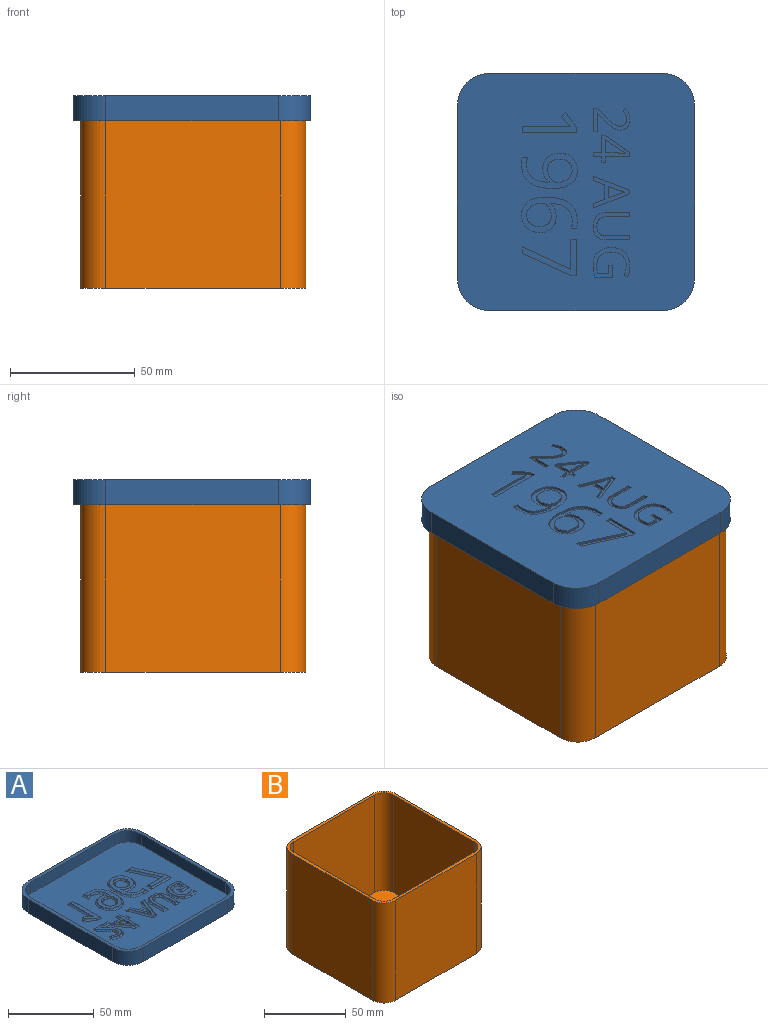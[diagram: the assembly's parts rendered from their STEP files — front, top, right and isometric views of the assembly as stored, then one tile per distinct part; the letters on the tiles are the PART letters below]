
ASSEMBLY  parts=2 mates=1
PART A: 347 faces, bbox 96x96x11 mm
  f0: plane 95x95mm, normal (0,0,-1), area 8042.6mm2, adj f2,f3,f4,f5,f6,f7,f8,f17
  f1: plane 91x91mm, normal (0,0,1), area 6700.1mm2, adj f9,f10,f11,f12,f13,f14,f15,f16
  f2: plane 69x10mm, normal (1,0,0), area 690mm2, adj f0,f3,f17,f18
  f3: cylinder r=13mm len=13mm, axis (0,0,-1), area 204.2mm2, adj f0,f2,f4,f18
  f4: plane 69x10mm, normal (0,1,0), area 690mm2, adj f0,f3,f5,f18
  f5: cylinder r=13mm len=13mm, axis (0,0,-1), area 204.2mm2, adj f0,f4,f6,f18
  f6: plane 69x10mm, normal (-1,0,0), area 690mm2, adj f0,f5,f7,f18
  f7: cylinder r=13mm len=13mm, axis (0,0,-1), area 204.2mm2, adj f0,f6,f8,f18
  f8: plane 69x10mm, normal (0,-1,0), area 690mm2, adj f0,f7,f17,f18
  f9: cylinder r=11mm len=11mm, axis (0,0,-1), area 138.2mm2, adj f1,f10,f16,f18
  f10: plane 69x8mm, normal (-1,0,0), area 552mm2, adj f1,f9,f11,f18
  f11: cylinder r=11mm len=11mm, axis (0,0,-1), area 138.2mm2, adj f1,f10,f12,f18
  f12: plane 69x8mm, normal (0,1,0), area 552mm2, adj f1,f11,f13,f18
  f13: cylinder r=11mm len=11mm, axis (0,0,-1), area 138.2mm2, adj f1,f12,f14,f18
  f14: plane 69x8mm, normal (1,0,0), area 552mm2, adj f1,f13,f15,f18
  f15: cylinder r=11mm len=11mm, axis (0,0,-1), area 138.2mm2, adj f1,f14,f16,f18
  f16: plane 69x8mm, normal (0,-1,0), area 552mm2, adj f1,f9,f15,f18
  f17: cylinder r=13mm len=13mm, axis (0,0,-1), area 204.2mm2, adj f0,f2,f8,f18
  f18: plane 95x95mm, normal (0,0,1), area 702.8mm2, adj f2,f3,f4,f5,f6,f7,f8,f9
  f19: plane 0.27x0.09mm, normal (1,0,0), area 0mm2, adj f20,f247,f249
  f20: plane 15.41x10.28mm, normal (0,0,1), area 45.3mm2, adj f19,f243,f246,f247,f248,f249,f250,f251
  f21: plane 5.35x1mm, normal (0,-1,0), area 5.3mm2, adj f22,f26,f27,f28
  f22: plane 6.38x4.48mm, normal (0.82,0.58,0), area 7.8mm2, adj f21,f23,f27,f28
  f23: extruded ~1.56x1mm, area 1.8mm2, adj f22,f24,f27,f28
  f24: plane 1x0.08mm, normal (0,1,0), area 0.1mm2, adj f23,f25,f27,f28
  f25: extruded ~3.17x1mm, area 3.2mm2, adj f24,f26,f27,f28
  f26: plane 4.77x1mm, normal (-1,0,0), area 4.8mm2, adj f21,f25,f27,f28
  f27: plane 14.42x10.67mm, normal (0,0,1), area 49.7mm2, adj f21,f22,f23,f24,f25,f26,f234,f235
  f28: plane 7.94x5.45mm, normal (0,0,1), area 20.5mm2, adj f21,f22,f23,f24,f25,f26
  f29: plane 14.5x12.81mm, normal (0,0,1), area 52.9mm2, adj f334,f335,f336,f337,f338,f339,f340,f341
  f30: plane 2.32x1.75mm, normal (0,0,1), area 2mm2, adj f344,f345,f346
  f31: plane 15.08x11.51mm, normal (0,0,1), area 54.1mm2, adj f284,f285,f286,f287,f288,f289,f290,f291
  f32: plane 15.42x12.61mm, normal (0,0,1), area 62.3mm2, adj f298,f299,f300,f301,f302,f303,f304,f305
  f33: plane 21.82x7.92mm, normal (0,0,1), area 64.6mm2, adj f318,f319,f320,f321,f322,f323,f324,f325
  f34: plane 0.42x0.21mm, normal (0,1,0), area 0mm2, adj f35,f223,f225
  f35: plane 22.92x14.78mm, normal (0,0,1), area 122.3mm2, adj f34,f219,f220,f221,f222,f223,f224,f225
  f36: plane 7.76x7.26mm, normal (0,0,1), area 45.7mm2, adj f274,f275,f276,f277,f278,f279,f280,f281
  f37: plane 0.42x0.2mm, normal (0,-1,0), area 0mm2, adj f38,f208,f210
  f38: plane 23.33x15.17mm, normal (0,0,1), area 122.1mm2, adj f37,f205,f206,f207,f208,f209,f210,f211
  f39: plane 7.79x7.21mm, normal (0,0,1), area 45.5mm2, adj f264,f265,f266,f267,f268,f269,f270,f271
  f40: plane 21.72x14.45mm, normal (0,0,1), area 83.5mm2, adj f327,f328,f329,f330,f331,f332,f333
  f41: plane 1.51x1mm, normal (-1,0,0), area 1.5mm2, adj f0,f42,f60,f61
  f42: plane 7.38x1mm, normal (0,1,0), area 7.4mm2, adj f0,f41,f43,f61
  f43: plane 1x0.08mm, normal (-1,0,0), area 0.1mm2, adj f0,f42,f44,f61
  f44: plane 3.14x3.07mm, normal (-0.7,-0.71,0), area 4.4mm2, adj f0,f43,f45,f61
  f45: extruded ~3.38x2.86mm, area 4.4mm2, adj f0,f44,f46,f61
  f46: extruded ~2.7x1mm, area 2.8mm2, adj f0,f45,f47,f61
  f47: extruded ~2.78x1.15mm, area 3.1mm2, adj f0,f46,f48,f61
  f48: extruded ~3.17x1.03mm, area 3.4mm2, adj f0,f47,f49,f61
  f49: extruded ~4.32x1.65mm, area 4.7mm2, adj f0,f48,f50,f61
  f50: plane 1.11x1mm, normal (0.79,-0.61,0), area 1.4mm2, adj f0,f49,f51,f61
  f51: extruded ~1.78x1.07mm, area 2.1mm2, adj f0,f50,f52,f61
  f52: extruded ~1.69x1mm, area 1.7mm2, adj f0,f51,f53,f61
  f53: extruded ~1.93x1mm, area 2.1mm2, adj f0,f52,f54,f61
  f54: extruded ~1.82x1mm, area 2mm2, adj f0,f53,f55,f61
  f55: extruded ~1.52x1mm, area 1.6mm2, adj f0,f54,f56,f61
  f56: extruded ~1.45x1mm, area 1.7mm2, adj f0,f55,f57,f61
  f57: extruded ~2.49x2.28mm, area 3.4mm2, adj f0,f56,f58,f61
  f58: plane 3.8x3.78mm, normal (0.71,0.71,0), area 5.4mm2, adj f0,f57,f59,f61
  f59: plane 1.4x1mm, normal (1,0,0), area 1.4mm2, adj f0,f58,f60,f61
  f60: plane 9.43x1mm, normal (0,-1,0), area 9.4mm2, adj f0,f41,f59,f61
  f61: plane 14.55x9.43mm, normal (0,0,-1), area 45.3mm2, adj f41,f42,f43,f44,f45,f46,f47,f48
  f62: extruded ~7.05x1.98mm, area 7.5mm2, adj f0,f63,f86,f87
  f63: extruded ~5.35x2.53mm, area 6.1mm2, adj f0,f62,f64,f87
  f64: extruded ~5x1.94mm, area 5.5mm2, adj f0,f63,f65,f87
  f65: extruded ~5.33x1.85mm, area 5.8mm2, adj f0,f64,f66,f87
  f66: extruded ~4.8x1.69mm, area 5.2mm2, adj f0,f65,f67,f87
  f67: extruded ~4.61x1.77mm, area 5.1mm2, adj f0,f66,f68,f87
  f68: extruded ~5.17x2.56mm, area 6mm2, adj f0,f67,f69,f87
  f69: plane 1x0.18mm, normal (0,1,0), area 0.2mm2, adj f0,f68,f70,f87
  f70: extruded ~6.84x2.02mm, area 7.3mm2, adj f0,f69,f71,f87
  f71: extruded ~5.34x2.17mm, area 6mm2, adj f0,f70,f72,f87
  f72: extruded ~2.61x1mm, area 2.7mm2, adj f0,f71,f73,f87
  f73: plane 2.13x1mm, normal (-1,0,0), area 2.1mm2, adj f0,f72,f74,f87
  f74: extruded ~2.64x1mm, area 2.7mm2, adj f0,f73,f75,f87
  f75: extruded ~7.36x3.17mm, area 8.3mm2, adj f0,f74,f86,f87
  f76: extruded ~2.49x1mm, area 2.6mm2, adj f77,f85,f87,f88
  f77: extruded ~2.09x1.69mm, area 2.7mm2, adj f76,f78,f87,f88
  f78: extruded ~2.85x1mm, area 2.9mm2, adj f77,f79,f87,f88
  f79: extruded ~2.01x1mm, area 2.1mm2, adj f78,f80,f87,f88
  f80: extruded ~1.78x1.52mm, area 2.4mm2, adj f79,f81,f87,f88
  f81: extruded ~2.45x1mm, area 2.5mm2, adj f80,f82,f87,f88
  f82: extruded ~3.24x1.23mm, area 3.6mm2, adj f81,f83,f87,f88
  f83: extruded ~3.39x1.08mm, area 3.6mm2, adj f82,f84,f87,f88
  f84: extruded ~3.84x1.16mm, area 4.1mm2, adj f83,f85,f87,f88
  f85: extruded ~3.28x1.33mm, area 3.7mm2, adj f76,f84,f87,f88
  f86: extruded ~9.57x2.49mm, area 10.1mm2, adj f0,f62,f75,f87
  f87: plane 22.33x14.17mm, normal (0,0,-1), area 122.1mm2, adj f62,f63,f64,f65,f66,f67,f68,f69
  f88: plane 9.79x9.21mm, normal (0,0,-1), area 72.7mm2, adj f76,f77,f78,f79,f80,f81,f82,f83
  f89: extruded ~5.13x1mm, area 5.2mm2, adj f0,f90,f114,f115
  f90: extruded ~3.31x2.55mm, area 4.2mm2, adj f0,f89,f91,f115
  f91: extruded ~3.87x1.14mm, area 4.1mm2, adj f0,f90,f92,f115
  f92: extruded ~4.98x1.96mm, area 5.5mm2, adj f0,f91,f93,f115
  f93: extruded ~5.35x1.89mm, area 5.8mm2, adj f0,f92,f94,f115
  f94: extruded ~4.81x1.69mm, area 5.2mm2, adj f0,f93,f95,f115
  f95: extruded ~4.58x1.72mm, area 5mm2, adj f0,f94,f96,f115
  f96: extruded ~3.04x1mm, area 3.1mm2, adj f0,f95,f97,f115
  f97: extruded ~2.17x1.88mm, area 2.9mm2, adj f0,f96,f98,f115
  f98: plane 1x0.18mm, normal (0,-1,0), area 0.2mm2, adj f0,f97,f99,f115
  f99: extruded ~6.76x1.98mm, area 7.2mm2, adj f0,f98,f100,f115
  f100: extruded ~5.39x2.21mm, area 6mm2, adj f0,f99,f101,f115
  f101: extruded ~2.7x1mm, area 2.7mm2, adj f0,f100,f102,f115
  f102: plane 2.13x1mm, normal (1,0,0), area 2.1mm2, adj f0,f101,f103,f115
  f103: extruded ~2.73x1mm, area 2.8mm2, adj f0,f102,f114,f115
  f104: extruded ~2.5x1mm, area 2.7mm2, adj f105,f113,f115,f116
  f105: extruded ~2.08x1.7mm, area 2.7mm2, adj f104,f106,f115,f116
  f106: extruded ~2.88x1mm, area 3mm2, adj f105,f107,f115,f116
  f107: extruded ~1.99x1mm, area 2.1mm2, adj f106,f108,f115,f116
  f108: extruded ~1.79x1.5mm, area 2.4mm2, adj f107,f109,f115,f116
  f109: extruded ~2.49x1mm, area 2.6mm2, adj f108,f110,f115,f116
  f110: extruded ~3.25x1.22mm, area 3.6mm2, adj f109,f111,f115,f116
  f111: extruded ~3.36x1.07mm, area 3.6mm2, adj f110,f112,f115,f116
  f112: extruded ~3.81x1.16mm, area 4.1mm2, adj f111,f113,f115,f116
  f113: extruded ~3.28x1.37mm, area 3.7mm2, adj f104,f112,f115,f116
  f114: extruded ~12.75x9.86mm, area 18.4mm2, adj f0,f89,f103,f115
  f115: plane 22.33x14.19mm, normal (0,0,-1), area 122.3mm2, adj f89,f90,f91,f92,f93,f94,f95,f96
  f116: plane 9.76x9.26mm, normal (0,0,-1), area 72.9mm2, adj f104,f105,f106,f107,f108,f109,f110,f111
  f117: plane 1.73x1mm, normal (0,-1,0), area 1.7mm2, adj f0,f118,f129,f130
  f118: plane 14.4x5.64mm, normal (-0.93,0.36,0), area 15.5mm2, adj f0,f117,f119,f130
  f119: plane 1.4x1mm, normal (0,1,0), area 1.4mm2, adj f0,f118,f120,f130
  f120: plane 14.4x5.67mm, normal (0.93,0.37,0), area 15.5mm2, adj f0,f119,f121,f130
  f121: plane 1.69x1mm, normal (0,-1,0), area 1.7mm2, adj f0,f120,f122,f130
  f122: plane 4.56x1.76mm, normal (-0.93,-0.36,0), area 4.9mm2, adj f0,f121,f123,f130
  f123: plane 5.75x1mm, normal (0,-1,0), area 5.7mm2, adj f0,f122,f129,f130
  f124: plane 4.64x1mm, normal (0,1,0), area 4.6mm2, adj f125,f128,f130,f131
  f125: plane 4.45x1.69mm, normal (-0.94,-0.35,0), area 4.8mm2, adj f124,f126,f130,f131
  f126: extruded ~2.07x1mm, area 2.2mm2, adj f125,f127,f130,f131
  f127: extruded ~2.07x1mm, area 2.2mm2, adj f126,f128,f130,f131
  f128: plane 4.45x1.67mm, normal (0.94,-0.35,0), area 4.7mm2, adj f124,f127,f130,f131
  f129: plane 4.56x1.79mm, normal (0.93,-0.36,0), area 4.9mm2, adj f0,f117,f123,f130
  f130: plane 14.4x12.72mm, normal (0,0,-1), area 52.9mm2, adj f117,f118,f119,f120,f121,f122,f123,f124
  f131: plane 6.51x4.64mm, normal (0,0,-1), area 14.4mm2, adj f124,f125,f126,f127,f128
  f132: plane 1.48x1mm, normal (-1,0,0), area 1.5mm2, adj f0,f133,f148,f149
  f133: plane 2.13x1mm, normal (0,1,0), area 2.1mm2, adj f0,f132,f134,f149
  f134: plane 9.64x1mm, normal (-1,0,0), area 9.6mm2, adj f0,f133,f135,f149
  f135: plane 1.73x1mm, normal (0,1,0), area 1.7mm2, adj f0,f134,f136,f149
  f136: plane 9.7x6.81mm, normal (0.82,0.57,0), area 11.9mm2, adj f0,f135,f137,f149
  f137: plane 1.42x1mm, normal (1,0,0), area 1.4mm2, adj f0,f136,f138,f149
  f138: plane 6.98x1mm, normal (0,-1,0), area 7mm2, adj f0,f137,f139,f149
  f139: plane 3.3x1mm, normal (1,0,0), area 3.3mm2, adj f0,f138,f140,f149
  f140: plane 1.56x1mm, normal (0,-1,0), area 1.6mm2, adj f0,f139,f141,f149
  f141: plane 3.3x1mm, normal (-1,0,0), area 3.3mm2, adj f0,f140,f148,f149
  f142: plane 5.35x1mm, normal (0,1,0), area 5.3mm2, adj f143,f147,f149,f150
  f143: plane 6.38x4.48mm, normal (-0.82,-0.58,0), area 7.8mm2, adj f142,f144,f149,f150
  f144: extruded ~1.56x1mm, area 1.8mm2, adj f143,f145,f149,f150
  f145: plane 1x0.08mm, normal (0,-1,0), area 0.1mm2, adj f144,f146,f149,f150
  f146: extruded ~3.17x1mm, area 3.2mm2, adj f145,f147,f149,f150
  f147: plane 4.77x1mm, normal (1,0,0), area 4.8mm2, adj f142,f146,f149,f150
  f148: plane 2.13x1mm, normal (0,-1,0), area 2.1mm2, adj f0,f132,f141,f149
  f149: plane 14.42x10.67mm, normal (0,0,-1), area 49.7mm2, adj f132,f133,f134,f135,f136,f137,f138,f139
  f150: plane 7.94x5.45mm, normal (0,0,-1), area 20.5mm2, adj f142,f143,f144,f145,f146,f147
  f151: plane 2.73x1mm, normal (0,-1,0), area 2.7mm2, adj f0,f152,f157,f158
  f152: plane 19.74x8.88mm, normal (-0.91,-0.41,0), area 21.6mm2, adj f0,f151,f153,f158
  f153: plane 1.98x1mm, normal (-1,0,0), area 2mm2, adj f0,f152,f154,f158
  f154: plane 14.45x1mm, normal (0,1,0), area 14.5mm2, adj f0,f153,f155,f158
  f155: plane 2.27x1mm, normal (1,0,0), area 2.3mm2, adj f0,f154,f156,f158
  f156: plane 11.84x1mm, normal (0,-1,0), area 11.8mm2, adj f0,f155,f157,f158
  f157: plane 19.45x9mm, normal (0.91,0.42,0), area 21.4mm2, adj f0,f151,f156,f158
  f158: plane 21.72x14.45mm, normal (0,0,-1), area 83.5mm2, adj f151,f152,f153,f154,f155,f156,f157
  f159: plane 21.72x1mm, normal (-1,0,0), area 21.7mm2, adj f0,f160,f167,f168
  f160: plane 2.08x1mm, normal (0,1,0), area 2.1mm2, adj f0,f159,f161,f168
  f161: plane 5.75x4.44mm, normal (0.61,0.79,0), area 7.3mm2, adj f0,f160,f162,f168
  f162: plane 1.69x1.31mm, normal (0.79,-0.61,0), area 2.1mm2, adj f0,f161,f163,f168
  f163: extruded ~3.53x2.9mm, area 4.6mm2, adj f0,f162,f164,f168
  f164: extruded ~1x0.7mm, area 1mm2, adj f0,f163,f165,f168
  f165: extruded ~3.66x1mm, area 3.7mm2, adj f0,f164,f166,f168
  f166: plane 15.48x1mm, normal (1,0,0), area 15.5mm2, adj f0,f165,f167,f168
  f167: plane 2.41x1mm, normal (0,-1,0), area 2.4mm2, adj f0,f159,f166,f168
  f168: plane 21.72x7.82mm, normal (0,0,-1), area 64.6mm2, adj f159,f160,f161,f162,f163,f164,f165,f166
  f169: plane 1.49x1mm, normal (1,0,0), area 1.5mm2, adj f0,f170,f188,f189
  f170: plane 3.21x1mm, normal (0,-1,0), area 3.2mm2, adj f0,f169,f171,f189
  f171: plane 4.41x1mm, normal (1,0,0), area 4.4mm2, adj f0,f170,f172,f189
  f172: extruded ~2.91x1mm, area 2.9mm2, adj f0,f171,f173,f189
  f173: extruded ~4.16x1.5mm, area 4.6mm2, adj f0,f172,f174,f189
  f174: extruded ~4.41x1.42mm, area 4.7mm2, adj f0,f173,f175,f189
  f175: extruded ~4.33x1.47mm, area 4.7mm2, adj f0,f174,f176,f189
  f176: extruded ~4.09x1.56mm, area 4.5mm2, adj f0,f175,f177,f189
  f177: extruded ~3.74x1mm, area 3.9mm2, adj f0,f176,f178,f189
  f178: plane 1.47x1mm, normal (-0.92,-0.4,0), area 1.6mm2, adj f0,f177,f179,f189
  f179: extruded ~4.28x1mm, area 4.4mm2, adj f0,f178,f180,f189
  f180: extruded ~3.95x1mm, area 4.1mm2, adj f0,f179,f181,f189
  f181: extruded ~2.59x2.57mm, area 3.7mm2, adj f0,f180,f182,f189
  f182: extruded ~3.92x1mm, area 4.1mm2, adj f0,f181,f183,f189
  f183: extruded ~5.43x1.81mm, area 5.9mm2, adj f0,f182,f184,f189
  f184: extruded ~5.07x1.94mm, area 5.6mm2, adj f0,f183,f185,f189
  f185: extruded ~2.73x1mm, area 2.7mm2, adj f0,f184,f186,f189
  f186: extruded ~2.32x1mm, area 2.4mm2, adj f0,f185,f187,f189
  f187: plane 6.98x1mm, normal (-1,0,0), area 7mm2, adj f0,f186,f188,f189
  f188: plane 4.88x1mm, normal (0,1,0), area 4.9mm2, adj f0,f169,f187,f189
  f189: plane 14.75x11.93mm, normal (0,0,-1), area 62.3mm2, adj f169,f170,f171,f172,f173,f174,f175,f176
  f190: plane 1.67x1mm, normal (0,1,0), area 1.7mm2, adj f0,f191,f203,f204
  f191: plane 9.34x1mm, normal (1,0,0), area 9.3mm2, adj f0,f190,f192,f204
  f192: extruded ~2.77x1mm, area 3mm2, adj f0,f191,f193,f204
  f193: extruded ~2.8x1mm, area 3mm2, adj f0,f192,f194,f204
  f194: extruded ~2.88x1mm, area 3.1mm2, adj f0,f193,f195,f204
  f195: extruded ~2.76x1mm, area 3mm2, adj f0,f194,f196,f204
  f196: plane 9.36x1mm, normal (-1,0,0), area 9.4mm2, adj f0,f195,f197,f204
  f197: plane 1.67x1mm, normal (0,1,0), area 1.7mm2, adj f0,f196,f198,f204
  f198: plane 9.24x1mm, normal (1,0,0), area 9.2mm2, adj f0,f197,f199,f204
  f199: extruded ~3.89x1.42mm, area 4.2mm2, adj f0,f198,f200,f204
  f200: extruded ~4.01x1.41mm, area 4.4mm2, adj f0,f199,f201,f204
  f201: extruded ~4.07x1.4mm, area 4.4mm2, adj f0,f200,f202,f204
  f202: extruded ~3.86x1.48mm, area 4.3mm2, adj f0,f201,f203,f204
  f203: plane 9.28x1mm, normal (-1,0,0), area 9.3mm2, adj f0,f190,f202,f204
  f204: plane 14.54x10.98mm, normal (0,0,-1), area 54.1mm2, adj f190,f191,f192,f193,f194,f195,f196,f197
  f205: bspline ~7.95x3.31mm, area 8.6mm2, adj f1,f38,f206,f207
  f206: bspline ~8.05x3.93mm, area 8.5mm2, adj f1,f38,f205,f208
  f207: bspline ~7.27x3.56mm, area 9.5mm2, adj f1,f38,f205,f209
  f208: bspline ~8.69x4.94mm, area 8.6mm2, adj f1,f37,f38,f206,f210
  f209: bspline ~8.72x4.22mm, area 9.1mm2, adj f1,f38,f207,f211
  f210: bspline ~8.13x3.47mm, area 9.6mm2, adj f1,f37,f38,f208,f212
  f211: bspline ~8.86x4.86mm, area 10.2mm2, adj f1,f38,f209,f213
  f212: bspline ~8.24x4.17mm, area 8.9mm2, adj f1,f38,f210,f214
  f213: bspline ~9.63x3.21mm, area 12.1mm2, adj f1,f38,f211,f215
  f214: bspline ~5x2.04mm, area 5.1mm2, adj f1,f38,f212,f216
  f215: bspline ~14.26x4.89mm, area 16.2mm2, adj f1,f38,f213,f217
  f216: cylinder r=1mm len=4.25mm, axis (0,-1,0), area 5mm2, adj f1,f38,f214,f218
  f217: bspline ~12.1x6.09mm, area 13.6mm2, adj f1,f38,f215,f218
  f218: bspline ~6.77x2.18mm, area 4.9mm2, adj f1,f38,f216,f217
  f219: bspline ~7.06x2.86mm, area 8.3mm2, adj f1,f35,f220,f221
  f220: bspline ~7.93x3.32mm, area 8.7mm2, adj f1,f35,f219,f222
  f221: bspline ~4.22x1.93mm, area 5.2mm2, adj f1,f35,f219,f223
  f222: bspline ~7.28x3.6mm, area 9.6mm2, adj f1,f35,f220,f224
  f223: bspline ~4.08x3.72mm, area 3.5mm2, adj f1,f34,f35,f221,f225
  f224: bspline ~7.39x4.24mm, area 9.1mm2, adj f1,f35,f222,f226
  f225: bspline ~8.26x3.44mm, area 9.5mm2, adj f1,f34,f35,f223,f227
  f226: bspline ~5.99x2.62mm, area 6.8mm2, adj f1,f35,f224,f228
  f227: bspline ~6.96x4.2mm, area 9mm2, adj f1,f35,f225,f229
  f228: bspline ~5.47x4.55mm, area 7mm2, adj f1,f35,f226,f230
  f229: bspline ~5.64x2.06mm, area 5.2mm2, adj f1,f35,f227,f231
  f230: bspline ~7.55x2.29mm, area 8.5mm2, adj f1,f35,f228,f232
  f231: cylinder r=1mm len=4.25mm, axis (0,1,0), area 5mm2, adj f1,f35,f229,f233
  f232: bspline ~15.75x14.97mm, area 29.8mm2, adj f1,f35,f230,f233
  f233: bspline ~4.54x1.69mm, area 5.1mm2, adj f1,f35,f231,f232
  f234: cylinder r=1mm len=3.48mm, axis (0,-1,0), area 3.9mm2, adj f1,f27,f235,f236
  f235: cylinder r=1mm len=3.13mm, axis (1,0,0), area 3.3mm2, adj f1,f27,f234,f237
  f236: cylinder r=1mm len=3.13mm, axis (-1,0,0), area 3.3mm2, adj f1,f27,f234,f238
  f237: cylinder r=1mm len=4.3mm, axis (0,-1,0), area 5.2mm2, adj f1,f27,f235,f239
  f238: cylinder r=1mm len=10.64mm, axis (0,-1,0), area 15.1mm2, adj f1,f27,f236,f240
  f239: cylinder r=1mm len=3.56mm, axis (1,0,0), area 4mm2, adj f1,f27,f237,f241
  f240: cylinder r=1mm len=3.25mm, axis (-1,0,0), area 3.9mm2, adj f1,f27,f238,f242
  f241: cylinder r=1mm len=4.3mm, axis (0,1,0), area 5.2mm2, adj f1,f27,f239,f244
  f242: cylinder r=1mm len=10.96mm, axis (-0.57,0.82,0), area 19.3mm2, adj f1,f27,f240,f245
  f243: cylinder r=1mm len=3.4mm, axis (0,-1,0), area 3.5mm2, adj f1,f20,f244,f246,f247
  f244: cylinder r=1mm len=7.87mm, axis (1,0,0), area 10.9mm2, adj f1,f27,f241,f243,f245,f247
  f245: cylinder r=1mm len=2.63mm, axis (0,1,0), area 3mm2, adj f1,f27,f242,f244,f247
  f246: cylinder r=1mm len=11.43mm, axis (1,0,0), area 16.4mm2, adj f1,f20,f243,f248
  f247: cylinder r=1mm len=8.27mm, axis (-1,0,0), area 10.8mm2, adj f1,f19,f20,f243,f244,f245,f249
  f248: cylinder r=1mm len=2.82mm, axis (0,1,0), area 3.3mm2, adj f1,f20,f246,f250
  f249: cylinder r=1mm len=3.86mm, axis (0.71,-0.7,0), area 5.7mm2, adj f1,f19,f20,f247,f251
  f250: cylinder r=1mm len=4.79mm, axis (-0.71,0.71,0), area 8.7mm2, adj f1,f20,f248,f252
  f251: bspline ~5.26x4.73mm, area 7.1mm2, adj f1,f20,f249,f253
  f252: bspline ~4.03x3.83mm, area 5.2mm2, adj f1,f20,f250,f254
  f253: bspline ~4.34x2.07mm, area 4.8mm2, adj f1,f20,f251,f255
  f254: bspline ~2.44x1.97mm, area 2.5mm2, adj f1,f20,f252,f256
  f255: bspline ~4.86x2.74mm, area 5.4mm2, adj f1,f20,f253,f257
  f256: bspline ~2.17x1.33mm, area 2.2mm2, adj f1,f20,f254,f258
  f257: bspline ~5.41x2.42mm, area 5.8mm2, adj f1,f20,f255,f259
  f258: bspline ~2.87x1.69mm, area 2.7mm2, adj f1,f20,f256,f260
  f259: bspline ~11.26x6.95mm, area 8.6mm2, adj f1,f20,f257,f261
  f260: bspline ~2.45x1.46mm, area 2.9mm2, adj f1,f20,f258,f262
  f261: cylinder r=1mm len=3.28mm, axis (0.61,0.79,0), area 3.8mm2, adj f1,f20,f259,f263
  f262: bspline ~2.39x1.36mm, area 2.5mm2, adj f1,f20,f260,f263
  f263: bspline ~4.21x3.39mm, area 3.9mm2, adj f1,f20,f261,f262
  f264: bspline ~5.92x2.41mm, area 6mm2, adj f38,f39,f265,f266
  f265: bspline ~4.9x2.73mm, area 5.2mm2, adj f38,f39,f264,f267
  f266: bspline ~5.14x2.26mm, area 5.3mm2, adj f38,f39,f264,f268
  f267: bspline ~3.43x1.89mm, area 3.8mm2, adj f38,f39,f265,f269
  f268: bspline ~4.14x2.62mm, area 5.1mm2, adj f38,f39,f266,f270
  f269: bspline ~3.37x2.98mm, area 4mm2, adj f38,f39,f267,f271
  f270: bspline ~3.45x1.68mm, area 3.7mm2, adj f38,f39,f268,f272
  f271: bspline ~3.54x1.75mm, area 4.4mm2, adj f38,f39,f269,f273
  f272: bspline ~2.96x2.72mm, area 3.4mm2, adj f38,f39,f270,f273
  f273: bspline ~2.74x1.71mm, area 3mm2, adj f38,f39,f271,f272
  f274: bspline ~2.72x1.7mm, area 3mm2, adj f35,f36,f275,f276
  f275: bspline ~2.77x2.4mm, area 3.4mm2, adj f35,f36,f274,f277
  f276: bspline ~3.58x1.77mm, area 4.4mm2, adj f35,f36,f274,f278
  f277: bspline ~3.5x1.68mm, area 3.8mm2, adj f35,f36,f275,f279
  f278: bspline ~2.96x2.82mm, area 4mm2, adj f35,f36,f276,f280
  f279: bspline ~4.42x2.07mm, area 5.1mm2, adj f35,f36,f277,f281
  f280: bspline ~3.47x1.88mm, area 3.8mm2, adj f35,f36,f278,f282
  f281: bspline ~5.11x2.24mm, area 5.3mm2, adj f35,f36,f279,f283
  f282: bspline ~4.16x2.74mm, area 5.3mm2, adj f35,f36,f280,f283
  f283: bspline ~5.91x2.41mm, area 6mm2, adj f35,f36,f281,f282
  f284: cylinder r=1mm len=10.28mm, axis (0,-1,0), area 15.4mm2, adj f1,f31,f285,f286
  f285: cylinder r=1mm len=3.67mm, axis (-1,0,0), area 4.2mm2, adj f1,f31,f284,f287
  f286: bspline ~5.79x3.41mm, area 7.1mm2, adj f1,f31,f284,f288
  f287: cylinder r=1mm len=10.34mm, axis (0,1,0), area 15.5mm2, adj f1,f31,f285,f289
  f288: bspline ~6.8x2.92mm, area 7.4mm2, adj f1,f31,f286,f290
  f289: bspline ~4.24x2.3mm, area 4.3mm2, adj f1,f31,f287,f291
  f290: bspline ~6.63x2.91mm, area 7.3mm2, adj f1,f31,f288,f292
  f291: bspline ~4.33x2.31mm, area 4.3mm2, adj f1,f31,f289,f293
  f292: bspline ~5.41x2.9mm, area 7.1mm2, adj f1,f31,f290,f294
  f293: bspline ~4.17x2.01mm, area 4.5mm2, adj f1,f31,f291,f295
  f294: cylinder r=1mm len=10.24mm, axis (0,1,0), area 15.3mm2, adj f1,f31,f292,f296
  f295: bspline ~4.21x2.29mm, area 4.3mm2, adj f1,f31,f293,f297
  f296: cylinder r=1mm len=3.67mm, axis (-1,0,0), area 4.2mm2, adj f1,f31,f294,f297
  f297: cylinder r=1mm len=10.36mm, axis (0,-1,0), area 15.5mm2, adj f1,f31,f295,f296
  f298: bspline ~5.97x2.29mm, area 6.7mm2, adj f1,f32,f299,f300
  f299: bspline ~7.43x3.54mm, area 9.6mm2, adj f1,f32,f298,f301
  f300: bspline ~4.48x4.46mm, area 6.2mm2, adj f1,f32,f298,f302
  f301: bspline ~6.85x3.59mm, area 9.2mm2, adj f1,f32,f299,f303
  f302: bspline ~5.45x1.98mm, area 6.7mm2, adj f1,f32,f300,f304
  f303: bspline ~3.97x1.27mm, area 4.4mm2, adj f1,f32,f301,f305
  f304: bspline ~9.02x3.25mm, area 7.9mm2, adj f1,f32,f302,f306
  f305: bspline ~4.77x2.14mm, area 4.4mm2, adj f1,f32,f303,f307
  f306: cylinder r=1mm len=3.7mm, axis (0.4,-0.92,0), area 4.1mm2, adj f1,f32,f304,f308
  f307: cylinder r=1mm len=8.71mm, axis (0,-1,0), area 12.3mm2, adj f1,f32,f305,f309
  f308: bspline ~7.63x2.98mm, area 6.6mm2, adj f1,f32,f306,f310
  f309: cylinder r=1mm len=6.88mm, axis (-1,0,0), area 9.2mm2, adj f1,f32,f307,f311
  f310: bspline ~5.41x3.25mm, area 6.6mm2, adj f1,f32,f308,f312
  f311: cylinder r=1mm len=3.49mm, axis (0,1,0), area 3.9mm2, adj f1,f32,f309,f313
  f312: bspline ~6.11x2.34mm, area 6.9mm2, adj f1,f32,f310,f314
  f313: cylinder r=1mm len=4.21mm, axis (1,0,0), area 5mm2, adj f1,f32,f311,f315
  f314: bspline ~6.69x2.72mm, area 7mm2, adj f1,f32,f312,f316
  f315: cylinder r=1mm len=4.41mm, axis (0,1,0), area 5.5mm2, adj f1,f32,f313,f317
  f316: bspline ~6.07x2.7mm, area 6.7mm2, adj f1,f32,f314,f317
  f317: bspline ~3.84x1.38mm, area 3.8mm2, adj f1,f32,f315,f316
  f318: cylinder r=1mm len=3.42mm, axis (-1,0,0), area 4.3mm2, adj f1,f33,f319,f320
  f319: cylinder r=1mm len=7.42mm, axis (-0.79,0.61,0), area 12.5mm2, adj f1,f33,f318,f321
  f320: cylinder r=1mm len=23.72mm, axis (0,-1,0), area 35.7mm2, adj f1,f33,f318,f322
  f321: cylinder r=1mm len=3.91mm, axis (0.61,0.79,0), area 4.9mm2, adj f1,f33,f319,f324
  f322: cylinder r=1mm len=4.41mm, axis (1,0,0), area 5.3mm2, adj f1,f33,f320,f325
  f323: bspline ~1.77x1.75mm, area 0.4mm2, adj f33,f324,f326
  f324: bspline ~8.9x7.51mm, area 7.5mm2, adj f1,f33,f321,f323,f326
  f325: cylinder r=1mm len=16.48mm, axis (0,1,0), area 25.1mm2, adj f1,f33,f322,f326
  f326: bspline ~5.42x1.18mm, area 4.2mm2, adj f1,f33,f323,f324,f325
  f327: cylinder r=1mm len=4.27mm, axis (0,1,0), area 5.1mm2, adj f1,f40,f328,f329
  f328: cylinder r=1mm len=16.45mm, axis (-1,0,0), area 24.3mm2, adj f1,f40,f327,f330
  f329: cylinder r=1mm len=12.84mm, axis (1,0,0), area 18.1mm2, adj f1,f40,f327,f331
  f330: cylinder r=1mm len=3.19mm, axis (0,-1,0), area 4.1mm2, adj f1,f40,f328,f332
  f331: cylinder r=1mm len=21.29mm, axis (-0.42,0.91,0), area 33.7mm2, adj f1,f40,f329,f333
  f332: cylinder r=1mm len=20.94mm, axis (0.41,-0.91,0), area 34.7mm2, adj f1,f40,f330,f333
  f333: cylinder r=1mm len=4.94mm, axis (1,0,0), area 6mm2, adj f1,f40,f331,f332
  f334: cylinder r=1mm len=3.84mm, axis (1,0,0), area 4.3mm2, adj f1,f29,f335,f336
  f335: cylinder r=1mm len=5.56mm, axis (0.36,-0.93,0), area 7.7mm2, adj f1,f29,f334,f337
  f336: cylinder r=1mm len=16.77mm, axis (-0.37,0.93,0), area 26mm2, adj f1,f29,f334,f338
  f337: cylinder r=1mm len=5.75mm, axis (1,0,0), area 8mm2, adj f1,f29,f335,f339
  f338: cylinder r=1mm len=2.77mm, axis (-1,0,0), area 3.3mm2, adj f1,f29,f336,f340
  f339: cylinder r=1mm len=5.56mm, axis (0.36,0.93,0), area 7.7mm2, adj f1,f29,f337,f341
  f340: cylinder r=1mm len=16.77mm, axis (-0.36,-0.93,0), area 26mm2, adj f1,f29,f338,f341
  f341: cylinder r=1mm len=3.87mm, axis (1,0,0), area 4.4mm2, adj f1,f29,f339,f340
  f342: bspline ~2.99x1.83mm, area 1.7mm2, adj f29,f343,f344,f345
  f343: bspline ~3.34x1.87mm, area 1.3mm2, adj f29,f342,f345
  f344: cylinder r=1mm len=4.8mm, axis (0.35,0.94,0), area 6.2mm2, adj f29,f30,f342,f345,f346
  f345: cylinder r=1mm len=4.81mm, axis (0.35,-0.94,0), area 6.5mm2, adj f29,f30,f342,f343,f344,f346
  f346: cylinder r=1mm len=4.64mm, axis (-1,0,0), area 5mm2, adj f29,f30,f344,f345
PART B: 19 faces, bbox 90x90x75 mm
  f0: plane 75x70mm, normal (1,0,0), area 5250mm2, adj f1,f15,f16,f17
  f1: cylinder r=10mm len=75mm, axis (0,0,-1), area 1178.1mm2, adj f0,f2,f16,f17
  f2: plane 75x70mm, normal (0,1,0), area 5250mm2, adj f1,f3,f16,f17
  f3: cylinder r=10mm len=75mm, axis (0,0,-1), area 1178.1mm2, adj f2,f4,f16,f17
  f4: plane 75x70mm, normal (-1,0,0), area 5250mm2, adj f3,f5,f16,f17
  f5: cylinder r=10mm len=75mm, axis (0,0,-1), area 1178.1mm2, adj f4,f6,f16,f17
  f6: plane 75x70mm, normal (0,-1,0), area 5250mm2, adj f5,f15,f16,f17
  f7: cylinder r=8mm len=73mm, axis (0,0,-1), area 917.3mm2, adj f8,f14,f16,f18
  f8: plane 73x70mm, normal (0,-1,0), area 5110mm2, adj f7,f9,f16,f18
  f9: cylinder r=8mm len=73mm, axis (0,0,-1), area 917.3mm2, adj f8,f10,f16,f18
  f10: plane 73x70mm, normal (-1,0,0), area 5110mm2, adj f9,f11,f16,f18
  f11: cylinder r=8mm len=73mm, axis (0,0,-1), area 917.3mm2, adj f10,f12,f16,f18
  f12: plane 73x70mm, normal (0,1,0), area 5110mm2, adj f11,f13,f16,f18
  f13: cylinder r=8mm len=73mm, axis (0,0,-1), area 917.3mm2, adj f12,f14,f16,f18
  f14: plane 73x70mm, normal (1,0,0), area 5110mm2, adj f7,f13,f16,f18
  f15: cylinder r=10mm len=75mm, axis (0,0,-1), area 1178.1mm2, adj f0,f6,f16,f17
  f16: plane 90x90mm, normal (0,0,1), area 673.1mm2, adj f0,f1,f2,f3,f4,f5,f6,f7
  f17: plane 90x90mm, normal (0,0,-1), area 8014.2mm2, adj f0,f1,f2,f3,f4,f5,f6,f15
  f18: plane 86x86mm, normal (0,0,1), area 7341.1mm2, adj f7,f8,f9,f10,f11,f12,f13,f14
PLACE A rot(axis=(0.71,-0.71,0),180deg) t=(-3,-2,77)mm
PLACE B at identity
MATE fastened A.f5 <-> B.f3  axis (0,0,-1) through (10,80,75)mm
